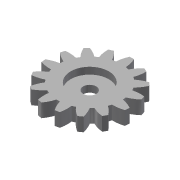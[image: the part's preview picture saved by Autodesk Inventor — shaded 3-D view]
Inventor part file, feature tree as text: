
AUTODESK INVENTOR PART (.ipt)
format: ipt  version: 2018 (Build 220112000, 112)  size: 238,592 bytes
history: native  units: mm
features: other x13, sketch x5, plane x4, extrude x1
ambient origin geometry x8: Origin, YZ Plane, XZ Plane, XY Plane, X Axis, Y Axis, Z Axis, Center Point
bodies: Volumenkörper1 (feature_tree)
feature tree (23):
  other  "Stirnzahnrad21_MIR.ipt"
  extrude  "Extrusion1"  Depth=14.0mm
  other  "Volumenkörper1::Stirnzahnrad21_MIR.ipt"
  other  "Bezeichnung1"
  sketch  "Sketch1"  dims[d0=10.0mm]
  sketch  "Sketch2"  dims[d16=40.0mm d17=0.0mm d41=0.0mm d43=40.0mm d46=40.0mm d47=0.0mm d48=0.0mm d1=14.0mm]
  sketch  "Skizze3"  dims[d2=2.5mm d3=0.0mm]
  sketch  "Skizze4"
  plane  "XZ Plane_1"
  plane  "Work Plane2"
  plane  "Work Plane8"
  plane  "Work Plane9"
  other  "Z Axis_1"
  other  "Flä1"
  sketch  "Skizze5"
  other  "Flä1::Abgeleitet"
  other  "Abstands-iMate"
  other  "Ausrichtungs-iMate"
  other  "Netz-iMate"
  other  "Achsen-iMate"
  other  "Positions-iMate"
  other  "Netz-iMate 2"
  other  "Startebenen-iMate"
